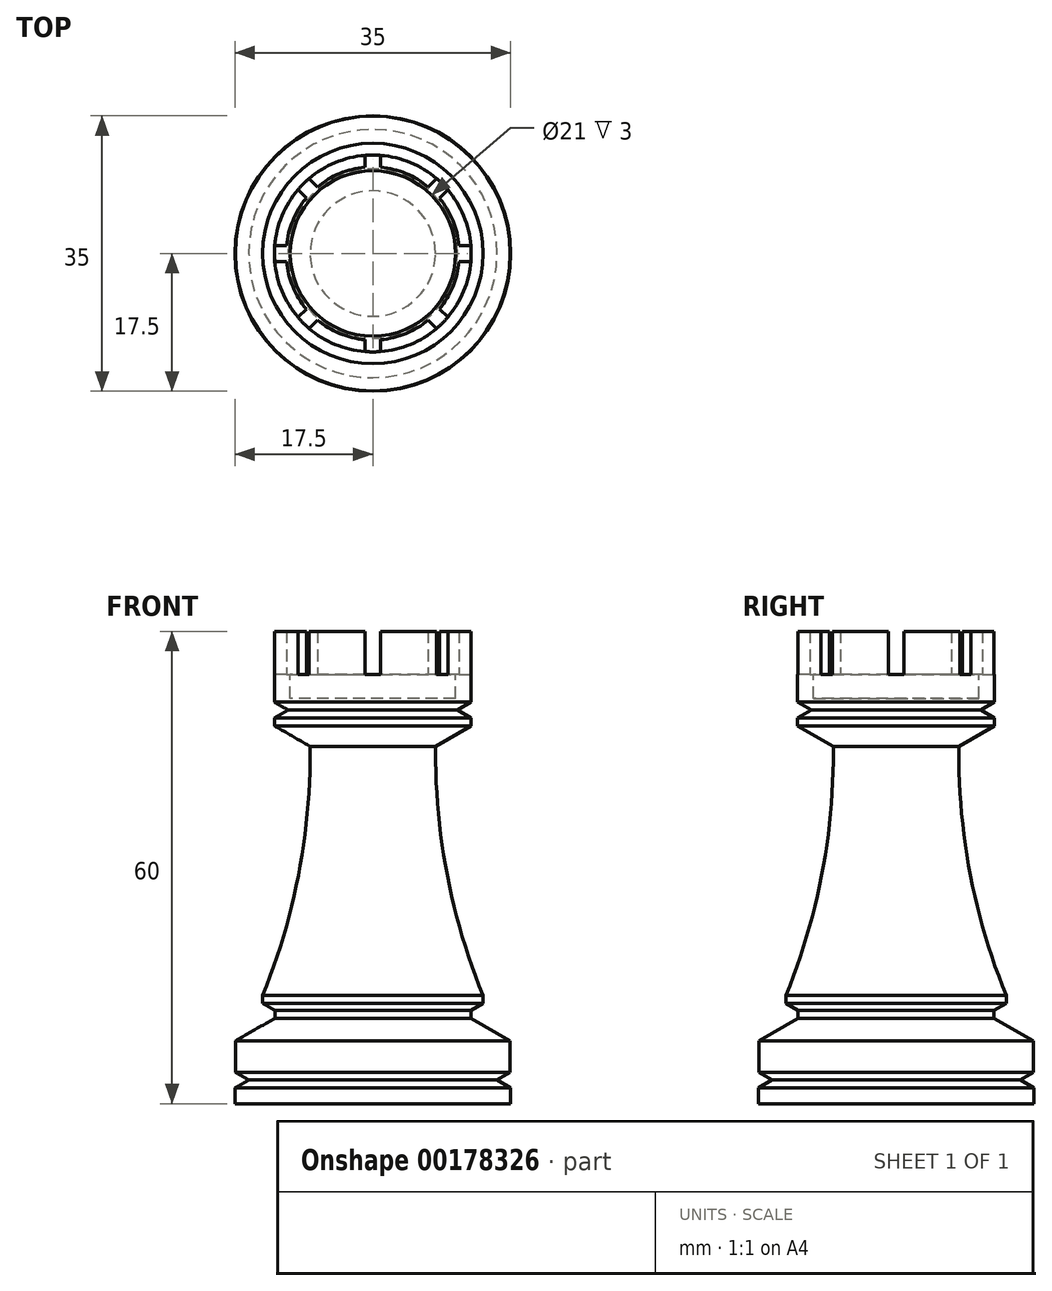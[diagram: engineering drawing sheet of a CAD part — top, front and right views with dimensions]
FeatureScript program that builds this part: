
annotation { "Feature Type Name" : "Feature", "Feature Type Description" : "" }
export const myFeature = defineFeature(function(context is Context, id is Id, definition is map)
    precondition{}
    {
        {
            var Q0;
            Q0=qCreatedBy(makeId("Front.planeOp"),FACE);
            var sketch = newSketch(context, id + "F0", { "sketchPlane" : qUnion([Q0])});
            skLineSegment(sketch, "E0", {"start": v(0, 0) * mm, "end": v(17.5, 0) * mm});
            skLineSegment(sketch, "E1", {"start": v(17.5, 0) * mm, "end": v(17.5, 2) * mm});
            skLineSegment(sketch, "E2", {"start": v(17.45, 3.97) * mm, "end": v(17.45, 7.97) * mm});
            skLineSegment(sketch, "E3", {"start": v(17.5, 2) * mm, "end": v(15.77, 3) * mm});
            skLineSegment(sketch, "E4", {"start": v(15.77, 3) * mm, "end": v(17.45, 3.97) * mm});
            skLineSegment(sketch, "E5", {"start": v(0, 0) * mm, "end": v(0, 6) * mm});
            skLineSegment(sketch, "E6", {"start": v(17.45, 7.97) * mm, "end": v(12.45, 10.86) * mm});
            skLineSegment(sketch, "E7.0", {"start": v(11, 60) * mm, "end": v(12.5, 60) * mm});
            skLineSegment(sketch, "E8.0", {"start": v(12.5, 60) * mm, "end": v(12.5, 51) * mm});
            skPoint(sketch, "E9.end.orphan", {"position": v(17.5, 3) * mm});
            skLineSegment(sketch, "E10.0", {"start": v(7.98, 43.46) * mm, "end": v(7.96, 45.38) * mm});
            skLineSegment(sketch, "E11", {"start": v(12.5, 48) * mm, "end": v(7.96, 45.38) * mm});
            skLineSegment(sketch, "E12", {"start": v(12.5, 49) * mm, "end": v(10.77, 50) * mm});
            skLineSegment(sketch, "E13", {"start": v(10.77, 50) * mm, "end": v(12.5, 51) * mm});
            skLineSegment(sketch, "E14.trimOffspring", {"start": v(12.5, 49) * mm, "end": v(12.5, 48) * mm});
            skPoint(sketch, "E15.visualSharp", {"position": v(7.98, 43.46) * mm});
            skPoint(sketch, "E16.orphan", {"position": v(0, 6) * mm});
            skLineSegment(sketch, "E17", {"start": v(0, 0) * mm, "end": v(0, 60) * mm});
            skLineSegment(sketch, "E18.0", {"start": v(0, 54.5) * mm, "end": v(11, 54.5) * mm});
            skLineSegment(sketch, "E19.0", {"start": v(11, 60) * mm, "end": v(11, 54.5) * mm});
            skLineSegment(sketch, "E20.0", {"start": v(12.45, 10.86) * mm, "end": v(12.45, 11.86) * mm});
            skLineSegment(sketch, "E21", {"start": v(12.45, 11.86) * mm, "end": v(14, 12.75) * mm});
            skLineSegment(sketch, "E22.0", {"start": v(14, 12.75) * mm, "end": v(14, 13.75) * mm});
            skPoint(sketch, "E23.end.orphan", {"position": v(0, 40.68) * mm});
            skPoint(sketch, "E24.3.internal.snap0", {"position": v(14.95, 9.41) * mm});
            skArc(sketch, "E25", {"start": v(7.98, 43.46) * mm, "mid": v(9.59, 28.32) * mm, "end": v(14, 13.75) * mm});
            skSolve(sketch);
        }
        {
            var Q0;
            {var subQ1=sQuery(id+"F0.wireOp",EDGE,"E0");Q0=makeQuery(id+"F0.imprint","IMPRINT",FACE,{"disambiguationData":[TD([[makeQuery(id+"F0.imprint","IMPRINT",EDGE,{"derivedFrom":subQ1}),1.0]])]});}
            var Q1;
            Q1=sQuery(id+"F0.wireOp",EDGE,"E17");
            revolve(context, id + "F1", {"entities" : qUnion([Q0]), "axis" : qUnion([Q1]), "revolveType" : RevolveType.FULL});
        }
        {
            var Q0;
            Q0=makeQuery(id+"F1.opRevolve","SWEPT_FACE",FACE,{"disambiguationData":[OSD([sQuery(id+"F0.wireOp",EDGE,"E18.0")])]});
            var sketch = newSketch(context, id + "F2", { "sketchPlane" : qUnion([Q0])});
            skLineSegment(sketch, "E26", {"start": v(0, 0) * mm, "end": v(33.12, 0) * mm});
            skLineSegment(sketch, "E27.0", {"start": v(0.41, -1) * mm, "end": v(33.12, -1) * mm});
            skLineSegment(sketch, "E28.0", {"start": v(0, 1) * mm, "end": v(33.12, 1) * mm});
            skLineSegment(sketch, "E29", {"start": v(0, 1) * mm, "end": v(-22.42, 1) * mm});
            skLineSegment(sketch, "E30", {"start": v(-22.42, 1) * mm, "end": v(-22.42, -1) * mm});
            skLineSegment(sketch, "E31", {"start": v(-22.42, -1) * mm, "end": v(0.41, -1) * mm});
            skLineSegment(sketch, "E32", {"start": v(33.12, 1) * mm, "end": v(33.12, -1) * mm});
            skLineSegment(sketch, "E33", {"start": v(0, 0) * mm, "end": v(0, 23.98) * mm});
            skLineSegment(sketch, "E34", {"start": v(0, 23.98) * mm, "end": v(-1, 23.98) * mm});
            skLineSegment(sketch, "E35", {"start": v(-1, 23.98) * mm, "end": v(-1, -22.24) * mm});
            skLineSegment(sketch, "E36", {"start": v(-1, -22.24) * mm, "end": v(1, -22.24) * mm});
            skLineSegment(sketch, "E37", {"start": v(1, -22.24) * mm, "end": v(1, 23.98) * mm});
            skLineSegment(sketch, "E38", {"start": v(1, 23.98) * mm, "end": v(0, 23.98) * mm});
            skLineSegment(sketch, "E39", {"start": v(0, 0) * mm, "end": v(21.43, 21.43) * mm});
            skLineSegment(sketch, "E40.0", {"start": v(0.7, -0.7) * mm, "end": v(22.14, 20.73) * mm});
            skLineSegment(sketch, "E41.0", {"start": v(-0.7, 0.7) * mm, "end": v(20.73, 22.14) * mm});
            skLineSegment(sketch, "E42", {"start": v(0.41, -1) * mm, "end": v(-22.47, -23.89) * mm});
            skLineSegment(sketch, "E43", {"start": v(-22.47, -23.89) * mm, "end": v(-23.89, -22.47) * mm});
            skLineSegment(sketch, "E44", {"start": v(-23.89, -22.47) * mm, "end": v(-0.7, 0.7) * mm});
            skLineSegment(sketch, "E45", {"start": v(20.73, 22.14) * mm, "end": v(22.14, 20.73) * mm});
            skLineSegment(sketch, "E46", {"start": v(0, 0) * mm, "end": v(-19.02, 19.02) * mm});
            skLineSegment(sketch, "E47", {"start": v(-18.31, 19.73) * mm, "end": v(21.43, -20.02) * mm});
            skLineSegment(sketch, "E48", {"start": v(21.43, -20.02) * mm, "end": v(20.02, -21.43) * mm});
            skLineSegment(sketch, "E49", {"start": v(20.02, -21.43) * mm, "end": v(-19.69, 18.27) * mm});
            skLineSegment(sketch, "E50", {"start": v(-19.69, 18.27) * mm, "end": v(-18.31, 19.73) * mm});
            skLineSegment(sketch, "E51", {"start": v(-18.31, 19.73) * mm, "end": v(-19.69, 18.27) * mm});
            skSolve(sketch);
        }
        {
            var Q0;
            Q0 = qSketchRegion(id + "F2", true);
            extrude(context, id + "F3", {"entities" : qUnion([Q0]), "operationType" : NewBodyOperationType.REMOVE, "depth" : 27 * mm});
        }
        {
            var Q0;
            Q0=makeQuery(id+"F3.boolean.opBoolean","MERGE",FACE,{"derivedFrom":[makeQuery(id+"F1.opRevolve","SWEPT_FACE",FACE,{"disambiguationData":[OSD([sQuery(id+"F0.wireOp",EDGE,"E18.0")])]}),makeQuery(id+"F3.opExtrude","CAP_FACE",FACE,{"disambiguationData":[OSD([sQuery(id+"F2.wireOp",EDGE,"E27.0"),sQuery(id+"F2.wireOp",EDGE,"E28.0"),sQuery(id+"F2.wireOp",EDGE,"E29"),sQuery(id+"F2.wireOp",EDGE,"E30"),sQuery(id+"F2.wireOp",EDGE,"E31"),sQuery(id+"F2.wireOp",EDGE,"E32"),sQuery(id+"F2.wireOp",EDGE,"E34"),sQuery(id+"F2.wireOp",EDGE,"E35"),sQuery(id+"F2.wireOp",EDGE,"E36"),sQuery(id+"F2.wireOp",EDGE,"E37"),sQuery(id+"F2.wireOp",EDGE,"E38"),sQuery(id+"F2.wireOp",EDGE,"E40.0"),sQuery(id+"F2.wireOp",EDGE,"E41.0"),sQuery(id+"F2.wireOp",EDGE,"E42"),sQuery(id+"F2.wireOp",EDGE,"E43"),sQuery(id+"F2.wireOp",EDGE,"E44"),sQuery(id+"F2.wireOp",EDGE,"E47"),sQuery(id+"F2.wireOp",EDGE,"E48"),sQuery(id+"F2.wireOp",EDGE,"E49"),sQuery(id+"F2.wireOp",EDGE,"E45"),sQuery(id+"F2.wireOp",EDGE,"E51")])],"isStart":true})]});
            var sketch = newSketch(context, id + "F4", { "sketchPlane" : qUnion([Q0])});
            skCircle(sketch, "E52", {"center": v(0, 0) * mm, "radius": 10.5 * mm});
            skSolve(sketch);
        }
        {
            var Q0;
            Q0 = qSketchRegion(id + "F4", true);
            extrude(context, id + "F5", {"entities" : qUnion([Q0]), "operationType" : NewBodyOperationType.REMOVE, "oppositeDirection" : true, "depth" : 3 * mm});
        }
    });
